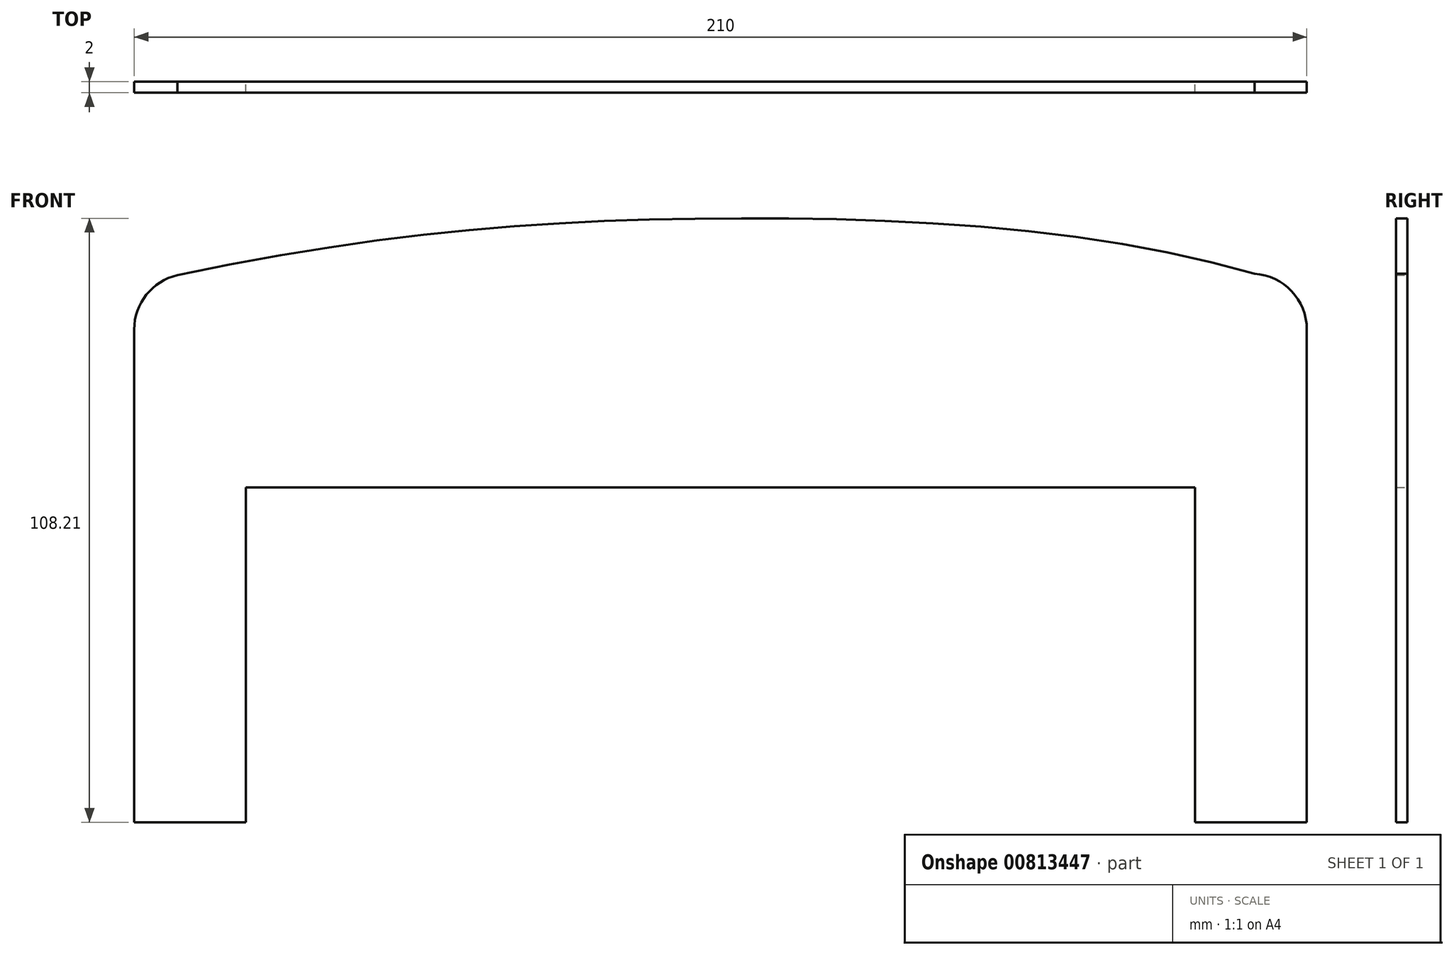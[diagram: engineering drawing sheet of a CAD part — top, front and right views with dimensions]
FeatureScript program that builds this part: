
annotation { "Feature Type Name" : "Feature", "Feature Type Description" : "" }
export const myFeature = defineFeature(function(context is Context, id is Id, definition is map)
    precondition{}
    {
        {
            var Q0;
            Q0=qCreatedBy(makeId("Front.planeOp"),FACE);
            var sketch = newSketch(context, id + "F0", { "sketchPlane" : qUnion([Q0])});
            skLineSegment(sketch, "E0.left", {"start": v(-105, 38.28) * mm, "end": v(-105, -50) * mm});
            skLineSegment(sketch, "E0.right", {"start": v(105, 38.28) * mm, "end": v(105, -50) * mm});
            skPoint(sketch, "E0.middle", {"position": v(0, 0) * mm});
            skPoint(sketch, "E1.visualSharp", {"position": v(-105, 50) * mm});
            skArc(sketch, "E1.filletArc", {"start": v(-97.28, 48.02) * mm, "mid": v(-102.84, 44.5) * mm, "end": v(-105, 38.28) * mm});
            skPoint(sketch, "E2.visualSharp", {"position": v(105, 50) * mm});
            skArc(sketch, "E2.filletArc", {"start": v(105, 38.28) * mm, "mid": v(102.3, 45.13) * mm, "end": v(95.64, 48.26) * mm});
            skFitSpline(sketch, "E3", {"points": [v(-97.28, 48.02) * mm, v(0, 58.19) * mm, v(95.64, 48.26) * mm], "startDerivative": vector(219.65, 46.24) * mm, "endDerivative": vector(172.4, -51.09) * mm});
            skLineSegment(sketch, "E4", {"start": v(-85, -50) * mm, "end": v(-85, 10) * mm});
            skLineSegment(sketch, "E5", {"start": v(85, -50) * mm, "end": v(85, 10) * mm});
            skLineSegment(sketch, "E6", {"start": v(-85, 10) * mm, "end": v(85, 10) * mm});
            skLineSegment(sketch, "E7", {"start": v(-105, -50) * mm, "end": v(-85, -50) * mm});
            skLineSegment(sketch, "E8", {"start": v(85, -50) * mm, "end": v(105, -50) * mm});
            skSolve(sketch);
        }
        {
            var Q0;
            Q0 = qSketchRegion(id + "F0", true);
            extrude(context, id + "F1", {"entities" : qUnion([Q0]), "depth" : 2 * mm, "offsetDistance" : 25 * mm});
        }
    });
